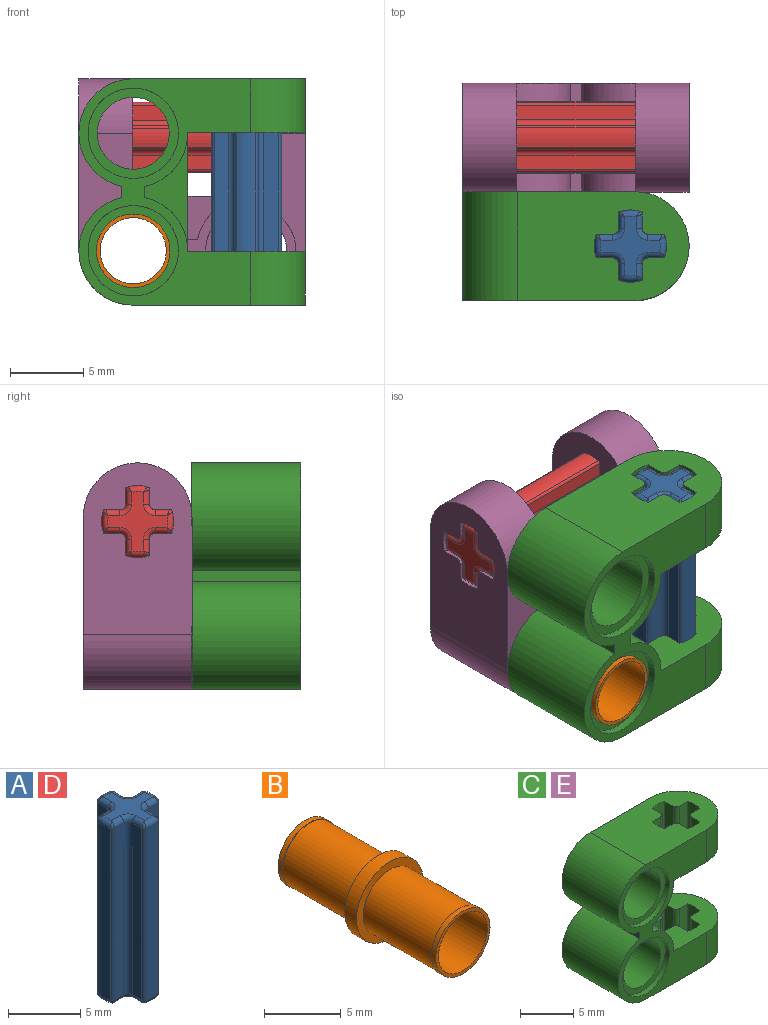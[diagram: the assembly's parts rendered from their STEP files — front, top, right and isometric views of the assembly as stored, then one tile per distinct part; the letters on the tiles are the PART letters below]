
ASSEMBLY  parts=5 mates=4
PART A: 74 faces, bbox 5.3x5.3x15.4 mm
  f0: cylinder r=2.44mm len=14.6mm, axis (0,0,-1), area 19.3mm2, adj f18,f25,f47,f72
  f1: plane 14.6x0.96mm, normal (0,1,0), area 14mm2, adj f2,f18,f48,f71
  f2: cylinder r=0.4mm len=14.6mm, axis (0,0,-1), area 9.2mm2, adj f1,f3,f46,f69
  f3: plane 14.6x0.96mm, normal (1,0,0), area 14mm2, adj f2,f19,f44,f67
  f4: cylinder r=2.44mm len=14.6mm, axis (0,0,-1), area 19.3mm2, adj f19,f20,f40,f63
  f5: plane 14.6x0.96mm, normal (-1,0,0), area 14mm2, adj f6,f20,f36,f59
  f6: cylinder r=0.4mm len=14.6mm, axis (0,0,-1), area 9.2mm2, adj f5,f7,f34,f57
  f7: plane 14.6x0.96mm, normal (0,1,0), area 14mm2, adj f6,f21,f32,f55
  f8: cylinder r=2.44mm len=14.6mm, axis (0,0,-1), area 19.3mm2, adj f21,f22,f28,f51
  f9: plane 14.6x0.96mm, normal (0,-1,0), area 14mm2, adj f10,f22,f27,f52
  f10: cylinder r=0.4mm len=14.6mm, axis (0,0,-1), area 9.2mm2, adj f9,f11,f29,f54
  f11: plane 14.6x0.96mm, normal (-1,0,0), area 14mm2, adj f10,f23,f31,f56
  f12: cylinder r=2.44mm len=14.6mm, axis (0,0,-1), area 19.3mm2, adj f23,f24,f35,f60
  f13: plane 14.6x0.96mm, normal (1,0,0), area 14mm2, adj f14,f24,f39,f64
  f14: cylinder r=0.4mm len=14.6mm, axis (0,0,-1), area 9.2mm2, adj f13,f15,f41,f66
  f15: plane 14.6x0.96mm, normal (0,-1,0), area 14mm2, adj f14,f25,f43,f68
  f16: plane 4.08x4.08mm, normal (0,0,1), area 6.4mm2, adj f27,f28,f29,f31,f32,f34,f35,f36
  f17: plane 4.08x4.08mm, normal (0,0,-1), area 6.4mm2, adj f51,f52,f54,f55,f56,f57,f59,f60
  f18: cylinder r=0.2mm len=14.6mm, axis (0,0,-1), area 3.8mm2, adj f0,f1,f49,f73
  f19: cylinder r=0.2mm len=14.6mm, axis (0,0,-1), area 3.8mm2, adj f3,f4,f42,f65
  f20: cylinder r=0.2mm len=14.6mm, axis (0,0,-1), area 3.8mm2, adj f4,f5,f38,f61
  f21: cylinder r=0.2mm len=14.6mm, axis (0,0,-1), area 3.8mm2, adj f7,f8,f30,f53
  f22: cylinder r=0.2mm len=14.6mm, axis (0,0,-1), area 3.8mm2, adj f8,f9,f26,f50
  f23: cylinder r=0.2mm len=14.6mm, axis (0,0,-1), area 3.8mm2, adj f11,f12,f33,f58
  f24: cylinder r=0.2mm len=14.6mm, axis (0,0,-1), area 3.8mm2, adj f12,f13,f37,f62
  f25: cylinder r=0.2mm len=14.6mm, axis (0,0,-1), area 3.8mm2, adj f0,f15,f45,f70
  f26: bspline ~0.49x0.4mm, area 0.1mm2, adj f22,f27,f28
  f27: cylinder r=0.4mm len=0.96mm, axis (1,0,0), area 0.6mm2, adj f9,f16,f26,f29
  f28: torus R=2.04mm, axis (0,0,-1), area 0.7mm2, adj f8,f16,f26,f30
  f29: torus R=0.8mm, axis (0,0,-1), area 0.5mm2, adj f10,f16,f27,f31
  f30: bspline ~0.49x0.4mm, area 0.1mm2, adj f21,f28,f32
  f31: cylinder r=0.4mm len=0.96mm, axis (0,-1,0), area 0.6mm2, adj f11,f16,f29,f33
  f32: cylinder r=0.4mm len=0.96mm, axis (-1,0,0), area 0.6mm2, adj f7,f16,f30,f34
  f33: bspline ~0.49x0.4mm, area 0.1mm2, adj f23,f31,f35
  f34: torus R=0.8mm, axis (0,0,-1), area 0.5mm2, adj f6,f16,f32,f36
  f35: torus R=2.04mm, axis (0,0,-1), area 0.7mm2, adj f12,f16,f33,f37
  f36: cylinder r=0.4mm len=0.96mm, axis (0,-1,0), area 0.6mm2, adj f5,f16,f34,f38
  f37: bspline ~0.49x0.4mm, area 0.1mm2, adj f24,f35,f39
  f38: bspline ~0.49x0.4mm, area 0.1mm2, adj f20,f36,f40
  f39: cylinder r=0.4mm len=0.96mm, axis (0,1,0), area 0.6mm2, adj f13,f16,f37,f41
  f40: torus R=2.04mm, axis (0,0,-1), area 0.7mm2, adj f4,f16,f38,f42
  f41: torus R=0.8mm, axis (0,0,-1), area 0.5mm2, adj f14,f16,f39,f43
  f42: bspline ~0.49x0.4mm, area 0.1mm2, adj f19,f40,f44
  f43: cylinder r=0.4mm len=0.96mm, axis (1,0,0), area 0.6mm2, adj f15,f16,f41,f45
  f44: cylinder r=0.4mm len=0.96mm, axis (0,1,0), area 0.6mm2, adj f3,f16,f42,f46
  f45: bspline ~0.49x0.4mm, area 0.1mm2, adj f25,f43,f47
  f46: torus R=0.8mm, axis (0,0,-1), area 0.5mm2, adj f2,f16,f44,f48
  f47: torus R=2.04mm, axis (0,0,-1), area 0.7mm2, adj f0,f16,f45,f49
  f48: cylinder r=0.4mm len=0.96mm, axis (-1,0,0), area 0.6mm2, adj f1,f16,f46,f49
  f49: bspline ~0.49x0.4mm, area 0.1mm2, adj f18,f47,f48
  f50: bspline ~0.49x0.4mm, area 0.1mm2, adj f22,f51,f52
  f51: torus R=2.04mm, axis (0,0,-1), area 0.7mm2, adj f8,f17,f50,f53
  f52: cylinder r=0.4mm len=0.96mm, axis (-1,0,0), area 0.6mm2, adj f9,f17,f50,f54
  f53: bspline ~0.49x0.4mm, area 0.1mm2, adj f21,f51,f55
  f54: torus R=0.8mm, axis (0,0,-1), area 0.5mm2, adj f10,f17,f52,f56
  f55: cylinder r=0.4mm len=0.96mm, axis (1,0,0), area 0.6mm2, adj f7,f17,f53,f57
  f56: cylinder r=0.4mm len=0.96mm, axis (0,1,0), area 0.6mm2, adj f11,f17,f54,f58
  f57: torus R=0.8mm, axis (0,0,-1), area 0.5mm2, adj f6,f17,f55,f59
  f58: bspline ~0.49x0.4mm, area 0.1mm2, adj f23,f56,f60
  f59: cylinder r=0.4mm len=0.96mm, axis (0,1,0), area 0.6mm2, adj f5,f17,f57,f61
  f60: torus R=2.04mm, axis (0,0,-1), area 0.7mm2, adj f12,f17,f58,f62
  f61: bspline ~0.49x0.4mm, area 0.1mm2, adj f20,f59,f63
  f62: bspline ~0.49x0.4mm, area 0.1mm2, adj f24,f60,f64
  f63: torus R=2.04mm, axis (0,0,-1), area 0.7mm2, adj f4,f17,f61,f65
  f64: cylinder r=0.4mm len=0.96mm, axis (0,-1,0), area 0.6mm2, adj f13,f17,f62,f66
  f65: bspline ~0.49x0.4mm, area 0.1mm2, adj f19,f63,f67
  f66: torus R=0.8mm, axis (0,0,-1), area 0.5mm2, adj f14,f17,f64,f68
  f67: cylinder r=0.4mm len=0.96mm, axis (0,-1,0), area 0.6mm2, adj f3,f17,f65,f69
  f68: cylinder r=0.4mm len=0.96mm, axis (-1,0,0), area 0.6mm2, adj f15,f17,f66,f70
  f69: torus R=0.8mm, axis (0,0,-1), area 0.5mm2, adj f2,f17,f67,f71
  f70: bspline ~0.49x0.4mm, area 0.1mm2, adj f25,f68,f72
  f71: cylinder r=0.4mm len=0.96mm, axis (1,0,0), area 0.6mm2, adj f1,f17,f69,f73
  f72: torus R=2.04mm, axis (0,0,-1), area 0.7mm2, adj f0,f17,f70,f73
  f73: bspline ~0.49x0.4mm, area 0.1mm2, adj f18,f71,f72
PART B: 12 faces, bbox 6.2x14.5x6.2 mm
  f0: plane 6.15x6.15mm, normal (0,-1,0), area 10.8mm2, adj f1,f11
  f1: cylinder r=3.08mm len=6.15mm, axis (0,1,0), area 20.6mm2, adj f0,f7
  f2: cylinder r=2.25mm len=14.53mm, axis (0,1,0), area 205.5mm2, adj f3,f8
  f3: plane 5x5mm, normal (0,1,0), area 3.7mm2, adj f2,f4
  f4: cylinder r=2.5mm len=5mm, axis (0,1,0), area 6.3mm2, adj f3,f5
  f5: plane 5x5mm, normal (0,-1,0), area 0.8mm2, adj f4,f6
  f6: cylinder r=2.45mm len=6.33mm, axis (0,1,0), area 97.5mm2, adj f5,f7
  f7: plane 6.15x6.15mm, normal (0,1,0), area 10.8mm2, adj f1,f6
  f8: plane 5x5mm, normal (0,-1,0), area 3.7mm2, adj f2,f9
  f9: cylinder r=2.5mm len=5mm, axis (0,-1,0), area 6.3mm2, adj f8,f10
  f10: plane 5x5mm, normal (0,1,0), area 0.8mm2, adj f9,f11
  f11: cylinder r=2.45mm len=6.33mm, axis (0,-1,0), area 97.5mm2, adj f0,f10
PART C: 60 faces, bbox 15.4x7.4x15.4 mm
  f0: plane 8x7.4mm, normal (0,0,1), area 40.2mm2, adj f5,f15,f16,f24,f28,f29,f30,f31
  f1: plane 8x7.4mm, normal (0,0,-1), area 40.2mm2, adj f6,f15,f16,f23,f44,f45,f46,f47
  f2: plane 11.7x7.4mm, normal (0,0,1), area 67.5mm2, adj f10,f15,f16,f23,f44,f45,f46,f47
  f3: plane 11.7x7.4mm, normal (0,0,-1), area 67.5mm2, adj f12,f15,f16,f24,f28,f29,f30,f31
  f4: plane 2.9x0.78mm, normal (1,0,0), area 2.2mm2, adj f5,f6,f16,f27
  f5: cylinder r=3.7mm len=7.4mm, axis (0,1,0), area 29.4mm2, adj f0,f4,f9,f15,f16,f25,f26,f27
  f6: cylinder r=3.7mm len=7.4mm, axis (0,1,0), area 29.4mm2, adj f1,f4,f9,f15,f16,f25,f26,f27
  f7: cylinder r=3.08mm len=6.15mm, axis (0,1,0), area 10.3mm2, adj f16,f21
  f8: cylinder r=3.08mm len=6.15mm, axis (0,1,0), area 10.3mm2, adj f16,f18
  f9: plane 2.9x0.78mm, normal (1,0,0), area 2.2mm2, adj f5,f6,f15,f26
  f10: cylinder r=3.7mm len=7.4mm, axis (0,1,0), area 80mm2, adj f2,f11,f15,f16
  f11: plane 7.4x0.78mm, normal (-1,0,0), area 5.7mm2, adj f10,f12,f15,f16
  f12: cylinder r=3.7mm len=7.4mm, axis (0,1,0), area 80mm2, adj f3,f11,f15,f16
  f13: cylinder r=3.08mm len=6.15mm, axis (0,1,0), area 10.3mm2, adj f15,f17
  f14: cylinder r=3.08mm len=6.15mm, axis (0,1,0), area 10.3mm2, adj f15,f20
  f15: plane 15.4x11.7mm, normal (0,-1,0), area 65mm2, adj f0,f1,f2,f3,f5,f6,f9,f10
  f16: plane 15.4x11.7mm, normal (0,1,0), area 65mm2, adj f0,f1,f2,f3,f4,f5,f6,f7
  f17: plane 6.15x6.15mm, normal (0,-1,0), area 10.8mm2, adj f13,f19
  f18: plane 6.15x6.15mm, normal (0,1,0), area 10.8mm2, adj f8,f19
  f19: cylinder r=2.45mm len=6.33mm, axis (0,1,0), area 97.5mm2, adj f17,f18
  f20: plane 6.15x6.15mm, normal (0,-1,0), area 10.8mm2, adj f14,f22
  f21: plane 6.15x6.15mm, normal (0,1,0), area 10.8mm2, adj f7,f22
  f22: cylinder r=2.45mm len=6.33mm, axis (0,1,0), area 97.5mm2, adj f20,f21
  f23: cylinder r=3.7mm len=7.4mm, axis (0,0,-1), area 42.5mm2, adj f1,f2,f15,f16
  f24: cylinder r=3.7mm len=7.4mm, axis (0,0,-1), area 42.5mm2, adj f0,f3,f15,f16
  f25: plane 7.92x1.6mm, normal (1,0,0), area 12.7mm2, adj f5,f6,f26,f27
  f26: plane 7.92x2.9mm, normal (0,-1,0), area 7.6mm2, adj f5,f6,f9,f25
  f27: plane 7.92x2.9mm, normal (0,1,0), area 7.6mm2, adj f4,f5,f6,f25
  f28: plane 3.66x1.12mm, normal (0,1,0), area 4.1mm2, adj f0,f3,f29,f43
  f29: cylinder r=0.4mm len=3.66mm, axis (0,0,-1), area 2.3mm2, adj f0,f3,f28,f30
  f30: plane 3.66x1.12mm, normal (-1,0,0), area 4.1mm2, adj f0,f3,f29,f31
  f31: cylinder r=2.46mm len=3.66mm, axis (0,0,-1), area 6mm2, adj f0,f3,f30,f32
  f32: plane 3.66x1.12mm, normal (1,0,0), area 4.1mm2, adj f0,f3,f31,f33
  f33: cylinder r=0.4mm len=3.66mm, axis (0,0,-1), area 2.3mm2, adj f0,f3,f32,f34
  f34: plane 3.66x1.12mm, normal (0,1,0), area 4.1mm2, adj f0,f3,f33,f35
  f35: cylinder r=2.46mm len=3.66mm, axis (0,0,-1), area 6mm2, adj f0,f3,f34,f36
  f36: plane 3.66x1.12mm, normal (0,-1,0), area 4.1mm2, adj f0,f3,f35,f37
  f37: cylinder r=0.4mm len=3.66mm, axis (0,0,-1), area 2.3mm2, adj f0,f3,f36,f38
  f38: plane 3.66x1.12mm, normal (1,0,0), area 4.1mm2, adj f0,f3,f37,f39
  f39: cylinder r=2.46mm len=3.66mm, axis (0,0,-1), area 6mm2, adj f0,f3,f38,f40
  f40: plane 3.66x1.12mm, normal (-1,0,0), area 4.1mm2, adj f0,f3,f39,f41
  f41: cylinder r=0.4mm len=3.66mm, axis (0,0,-1), area 2.3mm2, adj f0,f3,f40,f42
  f42: plane 3.66x1.12mm, normal (0,-1,0), area 4.1mm2, adj f0,f3,f41,f43
  f43: cylinder r=2.46mm len=3.66mm, axis (0,0,-1), area 6mm2, adj f0,f3,f28,f42
  f44: cylinder r=2.46mm len=3.66mm, axis (0,0,-1), area 6mm2, adj f1,f2,f45,f59
  f45: plane 3.66x1.12mm, normal (0,-1,0), area 4.1mm2, adj f1,f2,f44,f46
  f46: cylinder r=0.4mm len=3.66mm, axis (0,0,-1), area 2.3mm2, adj f1,f2,f45,f47
  f47: plane 3.66x1.12mm, normal (-1,0,0), area 4.1mm2, adj f1,f2,f46,f48
  f48: cylinder r=2.46mm len=3.66mm, axis (0,0,-1), area 6mm2, adj f1,f2,f47,f49
  f49: plane 3.66x1.12mm, normal (1,0,0), area 4.1mm2, adj f1,f2,f48,f50
  f50: cylinder r=0.4mm len=3.66mm, axis (0,0,-1), area 2.3mm2, adj f1,f2,f49,f51
  f51: plane 3.66x1.12mm, normal (0,-1,0), area 4.1mm2, adj f1,f2,f50,f52
  f52: cylinder r=2.46mm len=3.66mm, axis (0,0,-1), area 6mm2, adj f1,f2,f51,f53
  f53: plane 3.66x1.12mm, normal (0,1,0), area 4.1mm2, adj f1,f2,f52,f54
  f54: cylinder r=0.4mm len=3.66mm, axis (0,0,-1), area 2.3mm2, adj f1,f2,f53,f55
  f55: plane 3.66x1.12mm, normal (1,0,0), area 4.1mm2, adj f1,f2,f54,f56
  f56: cylinder r=2.46mm len=3.66mm, axis (0,0,-1), area 6mm2, adj f1,f2,f55,f57
  f57: plane 3.66x1.12mm, normal (-1,0,0), area 4.1mm2, adj f1,f2,f56,f58
  f58: cylinder r=0.4mm len=3.66mm, axis (0,0,-1), area 2.3mm2, adj f1,f2,f57,f59
  f59: plane 3.66x1.12mm, normal (0,1,0), area 4.1mm2, adj f1,f2,f44,f58
PART D: same geometry as A
PART E: same geometry as C
PLACE A at identity
PLACE B t=(0,7.4,0)mm
PLACE C at identity fixed
PLACE D rot(axis=(-0.58,-0.58,0.58),120deg) t=(-7.7,11.4,3.7)mm
PLACE E rot(axis=(0,-1,0),90deg) t=(-7.7,7.4,7.7)mm
MATE fastened D.f0 <-> E.f31  axis (1,0,0) through (-1.83,7.4,3.7)mm
MATE revolute E.f6 <-> B.f1  axis (0,1,0) through (-11.7,7.4,-4)mm
MATE fastened A.f0 <-> C.f31  axis (0,0,1) through (-4,0,0)mm
MATE fastened B.f1 <-> C.f5  axis (0,-1,0) through (-11.7,0,-4)mm
